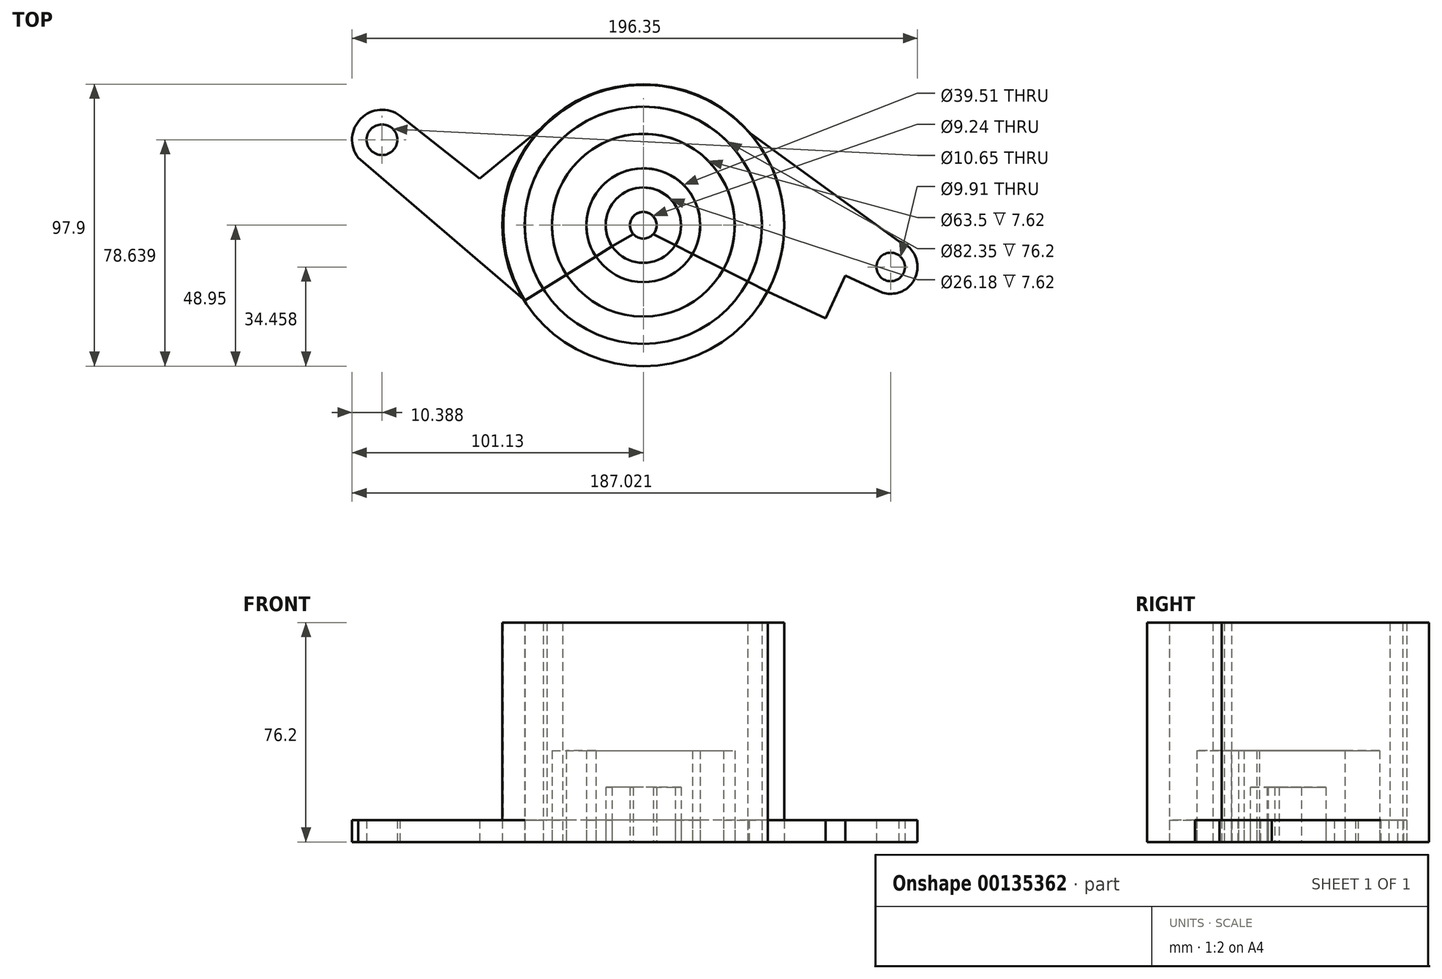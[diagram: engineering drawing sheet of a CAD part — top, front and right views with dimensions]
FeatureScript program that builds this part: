
annotation { "Feature Type Name" : "Feature", "Feature Type Description" : "" }
export const myFeature = defineFeature(function(context is Context, id is Id, definition is map)
    precondition{}
    {
        {
            var Q0;
            Q0=qCreatedBy(makeId("Top.planeOp"),FACE);
            var sketch = newSketch(context, id + "F0", { "sketchPlane" : qUnion([Q0])});
            skArc(sketch, "E0", {"start": v(3.44, -3.08) * mm, "mid": v(0, 4.62) * mm, "end": v(-3.44, -3.08) * mm});
            skArc(sketch, "E1", {"start": v(11.1, -6.94) * mm, "mid": v(-0.24, 13.09) * mm, "end": v(-10.85, -7.33) * mm});
            skLineSegment(sketch, "E2", {"start": v(-3.44, -3.08) * mm, "end": v(-10.85, -7.33) * mm});
            skLineSegment(sketch, "E3", {"start": v(3.44, -3.08) * mm, "end": v(11.1, -6.94) * mm});
            skArc(sketch, "E4", {"start": v(17.07, -9.94) * mm, "mid": v(-0.53, 19.75) * mm, "end": v(-16.52, -10.84) * mm});
            skArc(sketch, "E5", {"start": v(27.8, -15.33) * mm, "mid": v(-1.06, 31.73) * mm, "end": v(-26.71, -17.16) * mm});
            skArc(sketch, "E6", {"start": v(36.23, -19.57) * mm, "mid": v(-1.48, 41.15) * mm, "end": v(-34.73, -22.12) * mm});
            skArc(sketch, "E7", {"start": v(43.18, -23.06) * mm, "mid": v(-1.62, 48.7) * mm, "end": v(-41.14, -26.1) * mm});
            skLineSegment(sketch, "E8", {"start": v(-10.85, -7.33) * mm, "end": v(-41.14, -26.1) * mm});
            skLineSegment(sketch, "E9", {"start": v(11.1, -6.94) * mm, "end": v(43.18, -23.06) * mm});
            skLineSegment(sketch, "E10", {"start": v(-41.14, -26.1) * mm, "end": v(-99.35, 23.7) * mm});
            skArc(sketch, "E11", {"start": v(-84.12, 37.7) * mm, "mid": v(-99.35, 35.5) * mm, "end": v(-95.69, 20.56) * mm});
            skLineSegment(sketch, "E12", {"start": v(-84.49, 37.98) * mm, "end": v(-56.84, 16.13) * mm});
            skLineSegment(sketch, "E13", {"start": v(-56.84, 16.13) * mm, "end": v(-28.05, 39.77) * mm});
            skCircle(sketch, "E14", {"center": v(-90.74, 29.69) * mm, "radius": 5.32 * mm});
            skLineSegment(sketch, "E15", {"start": v(43.18, -23.06) * mm, "end": v(63.24, -32.37) * mm});
            skLineSegment(sketch, "E16", {"start": v(63.24, -32.37) * mm, "end": v(70.15, -17.47) * mm});
            skLineSegment(sketch, "E17", {"start": v(70.15, -17.47) * mm, "end": v(81.97, -22.95) * mm});
            skArc(sketch, "E18", {"start": v(81.97, -22.95) * mm, "mid": v(94.6, -17.85) * mm, "end": v(88.66, -5.59) * mm});
            skLineSegment(sketch, "E19", {"start": v(88.66, -5.59) * mm, "end": v(36.8, 32.14) * mm});
            skCircle(sketch, "E20", {"center": v(85.9, -14.5) * mm, "radius": 4.95 * mm});
            skSolve(sketch);
        }
        {
            var Q0;
            {var subQ9=sQuery(id+"F0.wireOp",EDGE,"E6");Q0=makeQuery(id+"F0.imprint","IMPRINT",FACE,{"disambiguationData":[TD([[makeQuery(id+"F0.imprint","IMPRINT",EDGE,{"derivedFrom":subQ9}),-1.0]])]});}
            extrude(context, id + "F1", {"entities" : qUnion([Q0]), "depth" : 76.2 * mm});
        }
        {
            var Q0;
            {var subQ0=sQuery(id+"F0.wireOp",EDGE,"E4");Q0=makeQuery(id+"F0.imprint","IMPRINT",FACE,{"disambiguationData":[TD([[makeQuery(id+"F0.imprint","IMPRINT",EDGE,{"derivedFrom":subQ0}),-1.0]])]});}
            extrude(context, id + "F2", {"entities" : qUnion([Q0]), "depth" : 31.75 * mm});
        }
        {
            var Q0;
            Q0=makeQuery(id+"F0.imprint","IMPRINT",FACE,{"disambiguationData":[TD([[makeQuery(id+"F0.imprint","IMPRINT",EDGE,{"derivedFrom":sQuery(id+"F0.wireOp",EDGE,"E0")}),-1.0]])]});
            extrude(context, id + "F3", {"entities" : qUnion([Q0]), "depth" : 19.05 * mm});
        }
        {
            var Q0;
            {var subQ0=sQuery(id+"F0.wireOp",EDGE,"E1");Q0=makeQuery(id+"F0.imprint","IMPRINT",FACE,{"disambiguationData":[TD([[makeQuery(id+"F0.imprint","IMPRINT",EDGE,{"derivedFrom":subQ0}),-1.0]])]});}
            var Q1;
            {var subQ0=sQuery(id+"F0.wireOp",EDGE,"E5");Q1=makeQuery(id+"F0.imprint","IMPRINT",FACE,{"disambiguationData":[TD([[makeQuery(id+"F0.imprint","IMPRINT",EDGE,{"derivedFrom":subQ0}),-1.0]])]});}
            extrude(context, id + "F4", {"entities" : qUnion([Q0, Q1]), "depth" : 7.62 * mm});
        }
        {
            var Q0;
            Q0=makeQuery(id+"F0.imprint","IMPRINT",FACE,{"disambiguationData":[TD([[makeQuery(id+"F0.imprint","IMPRINT",EDGE,{"derivedFrom":sQuery(id+"F0.wireOp",EDGE,"E14")}),-1.0]])]});
            var Q1;
            {var subQ0=sQuery(id+"F0.wireOp",EDGE,"E15");Q1=makeQuery(id+"F0.imprint","IMPRINT",FACE,{"disambiguationData":[TD([[makeQuery(id+"F0.imprint","IMPRINT",EDGE,{"derivedFrom":subQ0}),1.0]])]});}
            extrude(context, id + "F5", {"entities" : qUnion([Q0, Q1]), "operationType" : NewBodyOperationType.ADD, "depth" : 7.62 * mm});
        }
        {
            var Q0;
            Q0=qCreatedBy(makeId("Front.planeOp"),FACE);
            var sketch = newSketch(context, id + "F6", { "sketchPlane" : qUnion([Q0])});
            skLineSegment(sketch, "E21", {"start": v(0, 0) * mm, "end": v(0, 84.14) * mm, "construction": true});
            skSolve(sketch);
        }
        {
            var Q0;
            Q0=makeQuery(id+"F3.opExtrude","SWEPT_FACE",FACE,{"disambiguationData":[OSD([sQuery(id+"F0.wireOp",EDGE,"E3")])]});
            var Q1;
            {var subQ0=sQuery(id+"F0.wireOp",EDGE,"E9");Q1=makeQuery(id+"F4.opExtrude","SWEPT_FACE",FACE,{"disambiguationData":[OSD([subQ0]),TDD([makeQuery(id+"F0.imprint","IMPRINT",EDGE,{"disambiguationData":[TD([[makeQuery(id+"F0.imprint","INTERSECT",VERTEX,{"derivedFrom":[sQuery(id+"F0.wireOp",EDGE,"E4"),subQ0]}),1.0]])],"derivedFrom":subQ0})])]});}
            var Q2;
            Q2=makeQuery(id+"F2.opExtrude","SWEPT_FACE",FACE,{"disambiguationData":[OSD([sQuery(id+"F0.wireOp",EDGE,"E9")])]});
            var Q3;
            {var subQ0=sQuery(id+"F0.wireOp",EDGE,"E9");Q3=makeQuery(id+"F4.opExtrude","SWEPT_FACE",FACE,{"disambiguationData":[OSD([subQ0]),TDD([makeQuery(id+"F0.imprint","IMPRINT",EDGE,{"disambiguationData":[TD([[makeQuery(id+"F0.imprint","INTERSECT",VERTEX,{"derivedFrom":[sQuery(id+"F0.wireOp",EDGE,"E5"),subQ0]}),-1.0]])],"derivedFrom":subQ0})])]});}
            var Q4;
            Q4=makeQuery(id+"F1.opExtrude","SWEPT_FACE",FACE,{"disambiguationData":[OSD([sQuery(id+"F0.wireOp",EDGE,"E9")])]});
            var Q5;
            Q5=sQuery(id+"F6.wireOp",EDGE,"E21");
            revolve(context, id + "F7", {"entities" : qUnion([Q0, Q1, Q2, Q3, Q4]), "axis" : qUnion([Q5]), "revolveType" : RevolveType.FULL});
        }
    });
